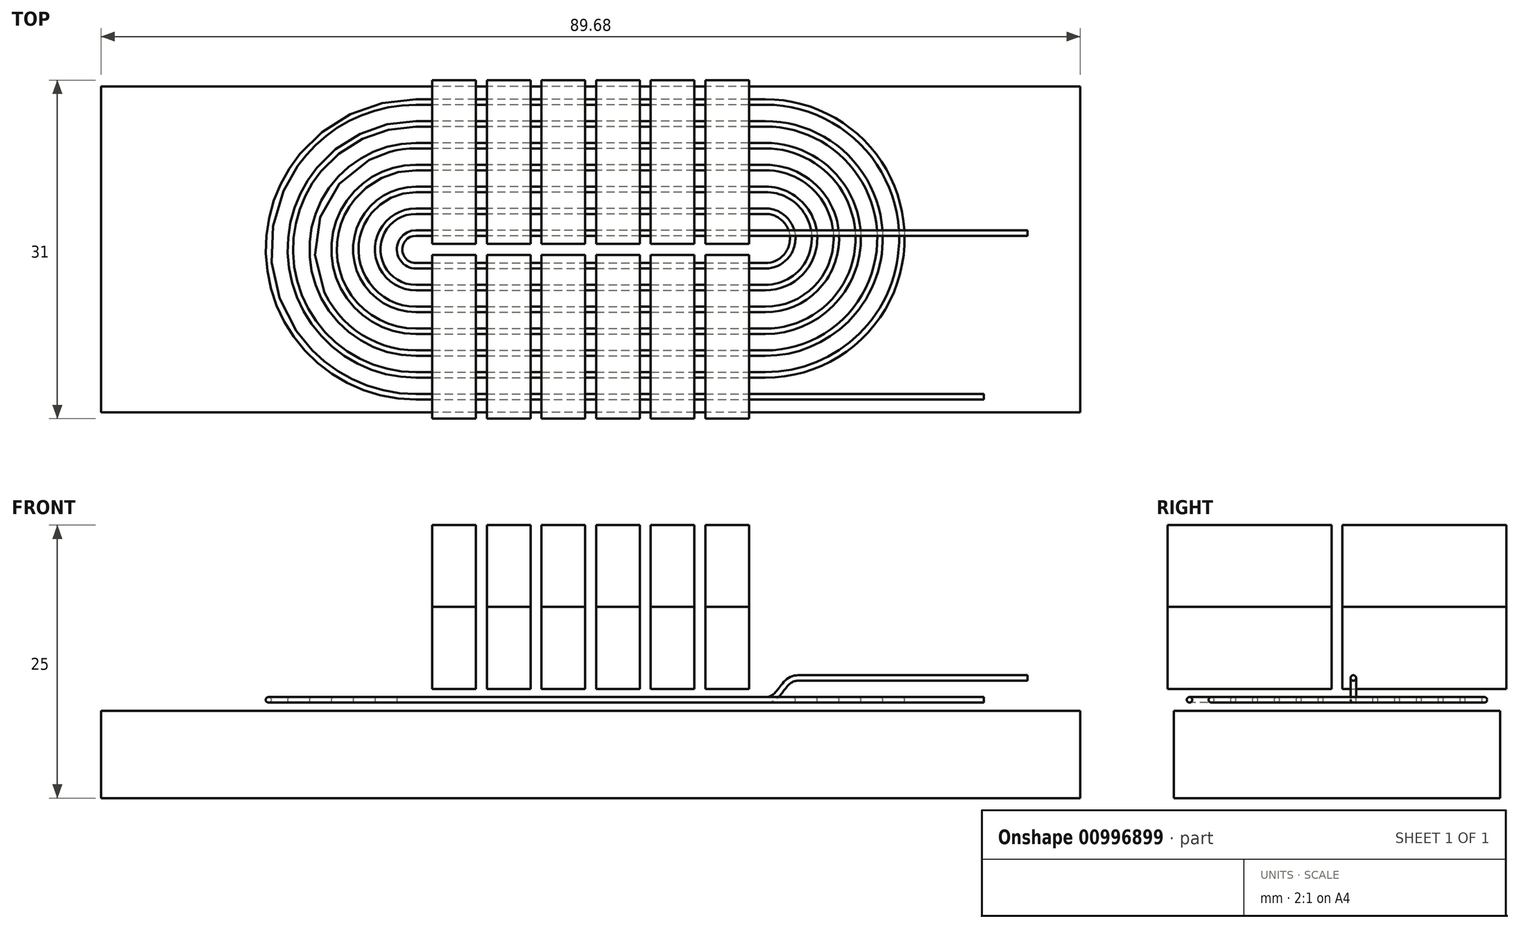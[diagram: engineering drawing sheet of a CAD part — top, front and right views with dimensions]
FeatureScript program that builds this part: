
annotation { "Feature Type Name" : "Feature", "Feature Type Description" : "" }
export const myFeature = defineFeature(function(context is Context, id is Id, definition is map)
    precondition{}
    {
        {
            var Q0;
            Q0=qCreatedBy(makeId("Top.planeOp"),FACE);
            cPlane(context, id + "F0", {"entities" : qUnion([Q0]), "cplaneType" : CPlaneType.OFFSET, "offset" : 1 * mm, "width" : 150 * mm, "height" : 150 * mm});
        }
        {
            var Q0;
            Q0=qCreatedBy(id+"F0.planeOp",FACE);
            var sketch = newSketch(context, id + "F1", { "sketchPlane" : qUnion([Q0])});
            skPoint(sketch, "E0.middle", {"position": v(0, 0) * mm});
            skLineSegment(sketch, "E1", {"start": v(0, 0) * mm, "end": v(0, 4.02) * mm, "construction": true});
            skLineSegment(sketch, "E2", {"start": v(0, 0) * mm, "end": v(5, 0) * mm, "construction": true});
            skPoint(sketch, "E3", {"position": v(0.5, 0.5) * mm});
            skLineSegment(sketch, "E4.bottom", {"start": v(0.5, 0.5) * mm, "end": v(4.5, 0.5) * mm});
            skLineSegment(sketch, "E4.top", {"start": v(0.5, 15.5) * mm, "end": v(4.5, 15.5) * mm});
            skLineSegment(sketch, "E4.left", {"start": v(0.5, 0.5) * mm, "end": v(0.5, 15.5) * mm});
            skLineSegment(sketch, "E4.right", {"start": v(4.5, 0.5) * mm, "end": v(4.5, 15.5) * mm});
            skLineSegment(sketch, "E5", {"start": v(5, 0) * mm, "end": v(5, 16.05) * mm, "construction": true});
            skLineSegment(sketch, "E6.MirrorCS", {"start": v(5.5, 0.5) * mm, "end": v(5.5, 15.5) * mm});
            skLineSegment(sketch, "E7.MirrorCS", {"start": v(9.5, 15.5) * mm, "end": v(5.5, 15.5) * mm});
            skLineSegment(sketch, "E8.MirrorCS", {"start": v(9.5, 0.5) * mm, "end": v(9.5, 15.5) * mm});
            skLineSegment(sketch, "E9.MirrorCS", {"start": v(9.5, 0.5) * mm, "end": v(5.5, 0.5) * mm});
            skLineSegment(sketch, "E10", {"start": v(7.5, 0.5) * mm, "end": v(7.5, 15.5) * mm, "construction": true});
            skLineSegment(sketch, "E11.MirrorCS", {"start": v(10.5, 0.5) * mm, "end": v(10.5, 15.5) * mm});
            skLineSegment(sketch, "E12.MirrorCS", {"start": v(14.5, 15.5) * mm, "end": v(10.5, 15.5) * mm});
            skLineSegment(sketch, "E13.MirrorCS", {"start": v(14.5, 0.5) * mm, "end": v(14.5, 15.5) * mm});
            skLineSegment(sketch, "E14.MirrorCS", {"start": v(14.5, 0.5) * mm, "end": v(10.5, 0.5) * mm});
            skLineSegment(sketch, "E15.MirrorCS", {"start": v(-10.5, 0.5) * mm, "end": v(-10.5, 15.5) * mm});
            skLineSegment(sketch, "E16.MirrorCS", {"start": v(-14.5, 0.5) * mm, "end": v(-14.5, 15.5) * mm});
            skLineSegment(sketch, "E17.MirrorCS", {"start": v(-0.5, 15.5) * mm, "end": v(-4.5, 15.5) * mm});
            skLineSegment(sketch, "E18.MirrorCS", {"start": v(-9.5, 0.5) * mm, "end": v(-9.5, 15.5) * mm});
            skLineSegment(sketch, "E19.MirrorCS", {"start": v(-5, 0) * mm, "end": v(-5, 16.05) * mm, "construction": true});
            skLineSegment(sketch, "E20.MirrorCS", {"start": v(-14.5, 15.5) * mm, "end": v(-10.5, 15.5) * mm});
            skLineSegment(sketch, "E21.MirrorCS", {"start": v(-14.5, 0.5) * mm, "end": v(-10.5, 0.5) * mm});
            skLineSegment(sketch, "E22.MirrorCS", {"start": v(-0.5, 0.5) * mm, "end": v(-0.5, 15.5) * mm});
            skLineSegment(sketch, "E23.MirrorCS", {"start": v(-5.5, 0.5) * mm, "end": v(-5.5, 15.5) * mm});
            skLineSegment(sketch, "E24.MirrorCS", {"start": v(-7.5, 0.5) * mm, "end": v(-7.5, 15.5) * mm, "construction": true});
            skLineSegment(sketch, "E25.MirrorCS", {"start": v(-4.5, 0.5) * mm, "end": v(-4.5, 15.5) * mm});
            skPoint(sketch, "E26.MirrorP", {"position": v(-0.5, 0.5) * mm});
            skLineSegment(sketch, "E27.MirrorCS", {"start": v(-0.5, 0.5) * mm, "end": v(-4.5, 0.5) * mm});
            skLineSegment(sketch, "E28.MirrorCS", {"start": v(-9.5, 0.5) * mm, "end": v(-5.5, 0.5) * mm});
            skLineSegment(sketch, "E29.MirrorCS", {"start": v(-9.5, 15.5) * mm, "end": v(-5.5, 15.5) * mm});
            skLineSegment(sketch, "E30.MirrorCS", {"start": v(10.5, -0.5) * mm, "end": v(10.5, -15.5) * mm});
            skLineSegment(sketch, "E31.MirrorCS", {"start": v(7.5, -0.5) * mm, "end": v(7.5, -15.5) * mm, "construction": true});
            skLineSegment(sketch, "E32.MirrorCS", {"start": v(14.5, -0.5) * mm, "end": v(14.5, -15.5) * mm});
            skLineSegment(sketch, "E33.MirrorCS", {"start": v(-10.5, -0.5) * mm, "end": v(-10.5, -15.5) * mm});
            skPoint(sketch, "E34.MirrorP", {"position": v(-0.5, -0.5) * mm});
            skLineSegment(sketch, "E35.MirrorCS", {"start": v(9.5, -0.5) * mm, "end": v(5.5, -0.5) * mm});
            skLineSegment(sketch, "E36.MirrorCS", {"start": v(-14.5, -0.5) * mm, "end": v(-14.5, -15.5) * mm});
            skLineSegment(sketch, "E37.MirrorCS", {"start": v(14.5, -15.5) * mm, "end": v(10.5, -15.5) * mm});
            skLineSegment(sketch, "E38.MirrorCS", {"start": v(9.5, -0.5) * mm, "end": v(9.5, -15.5) * mm});
            skLineSegment(sketch, "E39.MirrorCS", {"start": v(-0.5, -15.5) * mm, "end": v(-4.5, -15.5) * mm});
            skLineSegment(sketch, "E40.MirrorCS", {"start": v(14.5, -0.5) * mm, "end": v(10.5, -0.5) * mm});
            skLineSegment(sketch, "E41.MirrorCS", {"start": v(9.5, -15.5) * mm, "end": v(5.5, -15.5) * mm});
            skLineSegment(sketch, "E42.MirrorCS", {"start": v(-9.5, -0.5) * mm, "end": v(-9.5, -15.5) * mm});
            skPoint(sketch, "E43.MirrorP", {"position": v(0.5, -0.5) * mm});
            skLineSegment(sketch, "E44.MirrorCS", {"start": v(5.5, -0.5) * mm, "end": v(5.5, -15.5) * mm});
            skLineSegment(sketch, "E45.MirrorCS", {"start": v(-0.5, -0.5) * mm, "end": v(-4.5, -0.5) * mm});
            skLineSegment(sketch, "E46.MirrorCS", {"start": v(-9.5, -0.5) * mm, "end": v(-5.5, -0.5) * mm});
            skLineSegment(sketch, "E47.MirrorCS", {"start": v(-14.5, -0.5) * mm, "end": v(-10.5, -0.5) * mm});
            skLineSegment(sketch, "E48.MirrorCS", {"start": v(-9.5, -15.5) * mm, "end": v(-5.5, -15.5) * mm});
            skLineSegment(sketch, "E49.MirrorCS", {"start": v(-14.5, -15.5) * mm, "end": v(-10.5, -15.5) * mm});
            skLineSegment(sketch, "E50.MirrorCS", {"start": v(0.5, -15.5) * mm, "end": v(4.5, -15.5) * mm});
            skLineSegment(sketch, "E51.MirrorCS", {"start": v(5, 0) * mm, "end": v(5, -16.05) * mm, "construction": true});
            skLineSegment(sketch, "E52.MirrorCS", {"start": v(-0.5, -0.5) * mm, "end": v(-0.5, -15.5) * mm});
            skLineSegment(sketch, "E53.MirrorCS", {"start": v(4.5, -0.5) * mm, "end": v(4.5, -15.5) * mm});
            skLineSegment(sketch, "E54.MirrorCS", {"start": v(-5.5, -0.5) * mm, "end": v(-5.5, -15.5) * mm});
            skLineSegment(sketch, "E55.MirrorCS", {"start": v(-4.5, -0.5) * mm, "end": v(-4.5, -15.5) * mm});
            skLineSegment(sketch, "E56.MirrorCS", {"start": v(0.5, -0.5) * mm, "end": v(0.5, -15.5) * mm});
            skLineSegment(sketch, "E57.MirrorCS", {"start": v(-5, 0) * mm, "end": v(-5, -16.05) * mm, "construction": true});
            skLineSegment(sketch, "E58.MirrorCS", {"start": v(0.5, -0.5) * mm, "end": v(4.5, -0.5) * mm});
            skLineSegment(sketch, "E59.MirrorCS", {"start": v(0, 0) * mm, "end": v(0, -4.02) * mm, "construction": true});
            skLineSegment(sketch, "E60.MirrorCS", {"start": v(-7.5, -0.5) * mm, "end": v(-7.5, -15.5) * mm, "construction": true});
            skSolve(sketch);
        }
        {
            var Q0;
            Q0=qCreatedBy(makeId("Top.planeOp"),FACE);
            var sketch = newSketch(context, id + "F2", { "sketchPlane" : qUnion([Q0])});
            skLineSegment(sketch, "E61", {"start": v(16, 1.5) * mm, "end": v(0, 1.5) * mm});
            skLineSegment(sketch, "E62", {"start": v(0, 1.5) * mm, "end": v(-16, 1.5) * mm});
            skLineSegment(sketch, "E63.MirrorCS", {"start": v(0, -1.5) * mm, "end": v(-16, -1.5) * mm});
            skLineSegment(sketch, "E64.MirrorCS", {"start": v(0, -1.5) * mm, "end": v(16, -1.5) * mm});
            skArc(sketch, "E65", {"start": v(-16, 1.5) * mm, "mid": v(-17.5, 0) * mm, "end": v(-16, -1.5) * mm});
            skArc(sketch, "E66", {"start": v(16, -1.5) * mm, "mid": v(18.5, 1) * mm, "end": v(16, 3.5) * mm});
            skLineSegment(sketch, "E67", {"start": v(16, 3.5) * mm, "end": v(16, 1) * mm, "construction": true});
            skLineSegment(sketch, "E68", {"start": v(16, 1.5) * mm, "end": v(36, 1.5) * mm});
            skArc(sketch, "E69.0", {"start": v(16, -3.5) * mm, "mid": v(20.5, 1) * mm, "end": v(16, 5.5) * mm});
            skLineSegment(sketch, "E69.1", {"start": v(0, -3.5) * mm, "end": v(16, -3.5) * mm});
            skLineSegment(sketch, "E69.2", {"start": v(16, 3.5) * mm, "end": v(0, 3.5) * mm});
            skLineSegment(sketch, "E69.3", {"start": v(0, 3.5) * mm, "end": v(-16, 3.5) * mm});
            skArc(sketch, "E69.4", {"start": v(-16, 3.5) * mm, "mid": v(-19.5, 0) * mm, "end": v(-16, -3.5) * mm});
            skLineSegment(sketch, "E69.5", {"start": v(0, -3.5) * mm, "end": v(-16, -3.5) * mm});
            skArc(sketch, "E70.0", {"start": v(16, -5.5) * mm, "mid": v(22.5, 1) * mm, "end": v(16, 7.5) * mm});
            skLineSegment(sketch, "E70.1", {"start": v(0, -5.5) * mm, "end": v(16, -5.5) * mm});
            skLineSegment(sketch, "E70.2", {"start": v(16, 5.5) * mm, "end": v(0, 5.5) * mm});
            skLineSegment(sketch, "E70.3", {"start": v(0, 5.5) * mm, "end": v(-16, 5.5) * mm});
            skArc(sketch, "E70.4", {"start": v(-16, 5.5) * mm, "mid": v(-21.5, 0) * mm, "end": v(-16, -5.5) * mm});
            skLineSegment(sketch, "E70.5", {"start": v(0, -5.5) * mm, "end": v(-16, -5.5) * mm});
            skArc(sketch, "E71.0", {"start": v(16, -7.5) * mm, "mid": v(24.5, 1) * mm, "end": v(16, 9.5) * mm});
            skLineSegment(sketch, "E71.1", {"start": v(0, -7.5) * mm, "end": v(16, -7.5) * mm});
            skLineSegment(sketch, "E71.2", {"start": v(16, 7.5) * mm, "end": v(0, 7.5) * mm});
            skLineSegment(sketch, "E71.3", {"start": v(0, 7.5) * mm, "end": v(-16, 7.5) * mm});
            skArc(sketch, "E71.4", {"start": v(-16, 7.5) * mm, "mid": v(-23.5, 0) * mm, "end": v(-16, -7.5) * mm});
            skLineSegment(sketch, "E71.5", {"start": v(0, -7.5) * mm, "end": v(-16, -7.5) * mm});
            skArc(sketch, "E72.0", {"start": v(16, -9.5) * mm, "mid": v(26.5, 1) * mm, "end": v(16, 11.5) * mm});
            skLineSegment(sketch, "E72.1", {"start": v(0, -9.5) * mm, "end": v(16, -9.5) * mm});
            skLineSegment(sketch, "E72.2", {"start": v(0, -9.5) * mm, "end": v(-16, -9.5) * mm});
            skArc(sketch, "E72.3", {"start": v(-16, 9.5) * mm, "mid": v(-25.5, 0) * mm, "end": v(-16, -9.5) * mm});
            skLineSegment(sketch, "E73.0", {"start": v(0, 9.5) * mm, "end": v(-16, 9.5) * mm});
            skLineSegment(sketch, "E73.1", {"start": v(16, 9.5) * mm, "end": v(0, 9.5) * mm});
            skArc(sketch, "E74.0", {"start": v(16, -11.5) * mm, "mid": v(28.5, 1) * mm, "end": v(16, 13.5) * mm});
            skLineSegment(sketch, "E74.1", {"start": v(0, -11.5) * mm, "end": v(16, -11.5) * mm});
            skLineSegment(sketch, "E74.2", {"start": v(16, 11.5) * mm, "end": v(0, 11.5) * mm});
            skLineSegment(sketch, "E74.3", {"start": v(0, 11.5) * mm, "end": v(-16, 11.5) * mm});
            skArc(sketch, "E74.4", {"start": v(-16, 11.5) * mm, "mid": v(-27.5, 0) * mm, "end": v(-16, -11.5) * mm});
            skLineSegment(sketch, "E74.5", {"start": v(0, -11.5) * mm, "end": v(-16, -11.5) * mm});
            skLineSegment(sketch, "E75.1", {"start": v(0, -13.5) * mm, "end": v(16, -13.5) * mm});
            skLineSegment(sketch, "E75.2", {"start": v(16, 13.5) * mm, "end": v(0, 13.5) * mm});
            skLineSegment(sketch, "E75.3", {"start": v(0, 13.5) * mm, "end": v(-16, 13.5) * mm});
            skArc(sketch, "E75.4", {"start": v(-16, 13.5) * mm, "mid": v(-29.5, 0) * mm, "end": v(-16, -13.5) * mm});
            skLineSegment(sketch, "E75.5", {"start": v(0, -13.5) * mm, "end": v(-16, -13.5) * mm});
            skLineSegment(sketch, "E76", {"start": v(16, -13.5) * mm, "end": v(36, -13.5) * mm});
            skSolve(sketch);
        }
        {
            var Q0;
            Q0=sQuery(id+"F2.wireOp",EDGE,"E68");
            cPlane(context, id + "F3", {"entities" : qUnion([Q0]), "cplaneType" : CPlaneType.LINE_ANGLE, "offset" : 25 * mm, "angle" : 0 * degree, "width" : 150 * mm, "height" : 150 * mm});
        }
        {
            var Q0;
            Q0=qCreatedBy(makeId("Right.planeOp"),FACE);
            var sketch = newSketch(context, id + "F4", { "sketchPlane" : qUnion([Q0])});
            skCircle(sketch, "E77", {"center": v(-13.5, 0) * mm, "radius": 0.25 * mm});
            skSolve(sketch);
        }
        {
            var Q0;
            Q0=makeQuery(id+"F4.imprint","IMPRINT",FACE,{"disambiguationData":[TD([[makeQuery(id+"F4.imprint","IMPRINT",EDGE,{"derivedFrom":sQuery(id+"F4.wireOp",EDGE,"E77")}),1.0]])]});
            var Q1;
            Q1=sQuery(id+"F2.wireOp",EDGE,"E75.1");
            var Q2;
            Q2=sQuery(id+"F2.wireOp",EDGE,"E76");
            var Q3;
            Q3=sQuery(id+"F2.wireOp",EDGE,"E75.5");
            var Q4;
            Q4=sQuery(id+"F2.wireOp",EDGE,"E75.4");
            var Q5;
            Q5=sQuery(id+"F2.wireOp",EDGE,"E75.3");
            var Q6;
            Q6=sQuery(id+"F2.wireOp",EDGE,"E75.2");
            var Q7;
            Q7=sQuery(id+"F2.wireOp",EDGE,"E74.0");
            var Q8;
            Q8=sQuery(id+"F2.wireOp",EDGE,"E74.1");
            var Q9;
            Q9=sQuery(id+"F2.wireOp",EDGE,"E74.5");
            var Q10;
            Q10=sQuery(id+"F2.wireOp",EDGE,"E74.4");
            var Q11;
            Q11=sQuery(id+"F2.wireOp",EDGE,"E74.3");
            var Q12;
            Q12=sQuery(id+"F2.wireOp",EDGE,"E74.2");
            var Q13;
            Q13=sQuery(id+"F2.wireOp",EDGE,"E72.0");
            var Q14;
            Q14=sQuery(id+"F2.wireOp",EDGE,"E72.1");
            var Q15;
            Q15=sQuery(id+"F2.wireOp",EDGE,"E72.2");
            var Q16;
            Q16=sQuery(id+"F2.wireOp",EDGE,"E72.3");
            var Q17;
            Q17=sQuery(id+"F2.wireOp",EDGE,"E73.0");
            var Q18;
            Q18=sQuery(id+"F2.wireOp",EDGE,"E71.0");
            var Q19;
            Q19=sQuery(id+"F2.wireOp",EDGE,"E71.1");
            var Q20;
            Q20=sQuery(id+"F2.wireOp",EDGE,"E71.5");
            var Q21;
            Q21=sQuery(id+"F2.wireOp",EDGE,"E71.4");
            var Q22;
            Q22=sQuery(id+"F2.wireOp",EDGE,"E71.3");
            var Q23;
            Q23=sQuery(id+"F2.wireOp",EDGE,"E71.2");
            var Q24;
            Q24=sQuery(id+"F2.wireOp",EDGE,"E73.1");
            var Q25;
            Q25=sQuery(id+"F2.wireOp",EDGE,"E70.0");
            var Q26;
            Q26=sQuery(id+"F2.wireOp",EDGE,"E70.1");
            var Q27;
            Q27=sQuery(id+"F2.wireOp",EDGE,"E70.4");
            var Q28;
            Q28=sQuery(id+"F2.wireOp",EDGE,"E70.3");
            var Q29;
            Q29=sQuery(id+"F2.wireOp",EDGE,"E70.2");
            var Q30;
            Q30=sQuery(id+"F2.wireOp",EDGE,"E69.0");
            var Q31;
            Q31=sQuery(id+"F2.wireOp",EDGE,"E69.1");
            var Q32;
            Q32=sQuery(id+"F2.wireOp",EDGE,"E69.5");
            var Q33;
            Q33=sQuery(id+"F2.wireOp",EDGE,"E69.4");
            var Q34;
            Q34=sQuery(id+"F2.wireOp",EDGE,"E69.3");
            var Q35;
            Q35=sQuery(id+"F2.wireOp",EDGE,"E70.5");
            var Q36;
            Q36=sQuery(id+"F2.wireOp",EDGE,"E69.2");
            var Q37;
            Q37=sQuery(id+"F2.wireOp",EDGE,"E66");
            var Q38;
            Q38=sQuery(id+"F2.wireOp",EDGE,"E64.MirrorCS");
            var Q39;
            Q39=sQuery(id+"F2.wireOp",EDGE,"E63.MirrorCS");
            var Q40;
            Q40=sQuery(id+"F2.wireOp",EDGE,"E65");
            var Q41;
            Q41=sQuery(id+"F2.wireOp",EDGE,"E62");
            var Q42;
            Q42=sQuery(id+"F2.wireOp",EDGE,"E61");
            sweep(context, id + "F5", {"profiles" : qUnion([Q0]), "path" : qUnion([Q1, Q2, Q3, Q4, Q5, Q6, Q7, Q8, Q9, Q10, Q11, Q12, Q13, Q14, Q15, Q16, Q17, Q18, Q19, Q20, Q21, Q22, Q23, Q24, Q25, Q26, Q27, Q28, Q29, Q30, Q31, Q32, Q33, Q34, Q35, Q36, Q37, Q38, Q39, Q40, Q41, Q42])});
        }
        {
            var Q0;
            Q0=qCreatedBy(id+"F3.planeOp",FACE);
            var sketch = newSketch(context, id + "F6", { "sketchPlane" : qUnion([Q0])});
            skLineSegment(sketch, "E78.0", {"start": v(-19, 2) * mm, "end": v(-40, 2) * mm});
            skLineSegment(sketch, "E79", {"start": v(-19, 2) * mm, "end": v(-16, 2) * mm, "construction": true});
            skLineSegment(sketch, "E80", {"start": v(-17.5, 2) * mm, "end": v(-17.5, 0) * mm, "construction": true});
            skPoint(sketch, "E81", {"position": v(-17.5, 1) * mm});
            skFitSpline(sketch, "E82", {"points": [v(-16, 0) * mm, v(-17.5, 1) * mm, v(-19, 2) * mm], "startDerivative": vector(-4.5, 0) * mm, "endDerivative": vector(-4.5, 0) * mm});
            skLineSegment(sketch, "E83", {"start": v(-17.5, 2) * mm, "end": v(-19, 2) * mm, "construction": true});
            skLineSegment(sketch, "E84", {"start": v(-17.5, 0) * mm, "end": v(-16, 0) * mm, "construction": true});
            skSolve(sketch);
        }
        {
            var Q0;
            Q0=makeQuery(id+"F5.opSweep","CAP_FACE",FACE,{"disambiguationData":[OSD([sQuery(id+"F2.wireOp",VERTEX,"E61.start"),sQuery(id+"F4.wireOp",EDGE,"E77")])],"isStart":true});
            var Q1;
            Q1=sQuery(id+"F6.wireOp",EDGE,"E82");
            var Q2;
            Q2=sQuery(id+"F6.wireOp",EDGE,"E78.0");
            sweep(context, id + "F7", {"operationType" : NewBodyOperationType.ADD, "profiles" : qUnion([Q0]), "path" : qUnion([Q1, Q2])});
        }
        {
            var Q0;
            Q0=makeQuery(id+"F1.imprint","IMPRINT",FACE,{"disambiguationData":[TD([[makeQuery(id+"F1.imprint","IMPRINT",EDGE,{"derivedFrom":sQuery(id+"F1.wireOp",EDGE,"E33.MirrorCS")}),-1.0]])]});
            var Q1;
            Q1=makeQuery(id+"F1.imprint","IMPRINT",FACE,{"disambiguationData":[TD([[makeQuery(id+"F1.imprint","IMPRINT",EDGE,{"derivedFrom":sQuery(id+"F1.wireOp",EDGE,"E42.MirrorCS")}),1.0]])]});
            var Q2;
            Q2=makeQuery(id+"F1.imprint","IMPRINT",FACE,{"disambiguationData":[TD([[makeQuery(id+"F1.imprint","IMPRINT",EDGE,{"derivedFrom":sQuery(id+"F1.wireOp",EDGE,"E39.MirrorCS")}),-1.0]])]});
            var Q3;
            Q3=makeQuery(id+"F1.imprint","IMPRINT",FACE,{"disambiguationData":[TD([[makeQuery(id+"F1.imprint","IMPRINT",EDGE,{"derivedFrom":sQuery(id+"F1.wireOp",EDGE,"E50.MirrorCS")}),1.0]])]});
            var Q4;
            Q4=makeQuery(id+"F1.imprint","IMPRINT",FACE,{"disambiguationData":[TD([[makeQuery(id+"F1.imprint","IMPRINT",EDGE,{"derivedFrom":sQuery(id+"F1.wireOp",EDGE,"E35.MirrorCS")}),1.0]])]});
            var Q5;
            Q5=makeQuery(id+"F1.imprint","IMPRINT",FACE,{"disambiguationData":[TD([[makeQuery(id+"F1.imprint","IMPRINT",EDGE,{"derivedFrom":sQuery(id+"F1.wireOp",EDGE,"E30.MirrorCS")}),1.0]])]});
            var Q6;
            Q6=makeQuery(id+"F1.imprint","IMPRINT",FACE,{"disambiguationData":[TD([[makeQuery(id+"F1.imprint","IMPRINT",EDGE,{"derivedFrom":sQuery(id+"F1.wireOp",EDGE,"E11.MirrorCS")}),-1.0]])]});
            var Q7;
            Q7=makeQuery(id+"F1.imprint","IMPRINT",FACE,{"disambiguationData":[TD([[makeQuery(id+"F1.imprint","IMPRINT",EDGE,{"derivedFrom":sQuery(id+"F1.wireOp",EDGE,"E6.MirrorCS")}),-1.0]])]});
            var Q8;
            Q8=makeQuery(id+"F1.imprint","IMPRINT",FACE,{"disambiguationData":[TD([[makeQuery(id+"F1.imprint","IMPRINT",EDGE,{"derivedFrom":sQuery(id+"F1.wireOp",EDGE,"E4.bottom")}),1.0]])]});
            var Q9;
            Q9=makeQuery(id+"F1.imprint","IMPRINT",FACE,{"disambiguationData":[TD([[makeQuery(id+"F1.imprint","IMPRINT",EDGE,{"derivedFrom":sQuery(id+"F1.wireOp",EDGE,"E17.MirrorCS")}),1.0]])]});
            var Q10;
            Q10=makeQuery(id+"F1.imprint","IMPRINT",FACE,{"disambiguationData":[TD([[makeQuery(id+"F1.imprint","IMPRINT",EDGE,{"derivedFrom":sQuery(id+"F1.wireOp",EDGE,"E18.MirrorCS")}),-1.0]])]});
            var Q11;
            Q11=makeQuery(id+"F1.imprint","IMPRINT",FACE,{"disambiguationData":[TD([[makeQuery(id+"F1.imprint","IMPRINT",EDGE,{"derivedFrom":sQuery(id+"F1.wireOp",EDGE,"E15.MirrorCS")}),1.0]])]});
            extrude(context, id + "F8", {"entities" : qUnion([Q0, Q1, Q2, Q3, Q4, Q5, Q6, Q7, Q8, Q9, Q10, Q11]), "depth" : 7.5 * mm, "offsetDistance" : 25 * mm});
        }
        {
            var Q0;
            Q0=makeQuery(id+"F8.opExtrude","SWEPT_BODY",BODY,{"disambiguationData":[OSD([sQuery(id+"F1.wireOp",EDGE,"E15.MirrorCS"),sQuery(id+"F1.wireOp",EDGE,"E16.MirrorCS"),sQuery(id+"F1.wireOp",EDGE,"E20.MirrorCS"),sQuery(id+"F1.wireOp",EDGE,"E21.MirrorCS")])]});
            var Q1;
            Q1=makeQuery(id+"F8.opExtrude","SWEPT_BODY",BODY,{"disambiguationData":[OSD([sQuery(id+"F1.wireOp",EDGE,"E18.MirrorCS"),sQuery(id+"F1.wireOp",EDGE,"E23.MirrorCS"),sQuery(id+"F1.wireOp",EDGE,"E28.MirrorCS"),sQuery(id+"F1.wireOp",EDGE,"E29.MirrorCS")])]});
            var Q2;
            Q2=makeQuery(id+"F8.opExtrude","SWEPT_BODY",BODY,{"disambiguationData":[OSD([sQuery(id+"F1.wireOp",EDGE,"E17.MirrorCS"),sQuery(id+"F1.wireOp",EDGE,"E22.MirrorCS"),sQuery(id+"F1.wireOp",EDGE,"E25.MirrorCS"),sQuery(id+"F1.wireOp",EDGE,"E27.MirrorCS")])]});
            var Q3;
            Q3=makeQuery(id+"F8.opExtrude","SWEPT_BODY",BODY,{"disambiguationData":[OSD([sQuery(id+"F1.wireOp",EDGE,"E4.bottom"),sQuery(id+"F1.wireOp",EDGE,"E4.top"),sQuery(id+"F1.wireOp",EDGE,"E4.left"),sQuery(id+"F1.wireOp",EDGE,"E4.right")])]});
            var Q4;
            Q4=makeQuery(id+"F8.opExtrude","SWEPT_BODY",BODY,{"disambiguationData":[OSD([sQuery(id+"F1.wireOp",EDGE,"E11.MirrorCS"),sQuery(id+"F1.wireOp",EDGE,"E12.MirrorCS"),sQuery(id+"F1.wireOp",EDGE,"E13.MirrorCS"),sQuery(id+"F1.wireOp",EDGE,"E14.MirrorCS")])]});
            var Q5;
            Q5=makeQuery(id+"F8.opExtrude","SWEPT_BODY",BODY,{"disambiguationData":[OSD([sQuery(id+"F1.wireOp",EDGE,"E6.MirrorCS"),sQuery(id+"F1.wireOp",EDGE,"E7.MirrorCS"),sQuery(id+"F1.wireOp",EDGE,"E8.MirrorCS"),sQuery(id+"F1.wireOp",EDGE,"E9.MirrorCS")])]});
            var Q6;
            Q6=makeQuery(id+"F8.opExtrude","SWEPT_BODY",BODY,{"disambiguationData":[OSD([sQuery(id+"F1.wireOp",EDGE,"E30.MirrorCS"),sQuery(id+"F1.wireOp",EDGE,"E32.MirrorCS"),sQuery(id+"F1.wireOp",EDGE,"E37.MirrorCS"),sQuery(id+"F1.wireOp",EDGE,"E40.MirrorCS")])]});
            var Q7;
            Q7=makeQuery(id+"F8.opExtrude","SWEPT_BODY",BODY,{"disambiguationData":[OSD([sQuery(id+"F1.wireOp",EDGE,"E35.MirrorCS"),sQuery(id+"F1.wireOp",EDGE,"E38.MirrorCS"),sQuery(id+"F1.wireOp",EDGE,"E41.MirrorCS"),sQuery(id+"F1.wireOp",EDGE,"E44.MirrorCS")])]});
            var Q8;
            Q8=makeQuery(id+"F8.opExtrude","SWEPT_BODY",BODY,{"disambiguationData":[OSD([sQuery(id+"F1.wireOp",EDGE,"E39.MirrorCS"),sQuery(id+"F1.wireOp",EDGE,"E45.MirrorCS"),sQuery(id+"F1.wireOp",EDGE,"E52.MirrorCS"),sQuery(id+"F1.wireOp",EDGE,"E55.MirrorCS")])]});
            var Q9;
            Q9=makeQuery(id+"F8.opExtrude","SWEPT_BODY",BODY,{"disambiguationData":[OSD([sQuery(id+"F1.wireOp",EDGE,"E42.MirrorCS"),sQuery(id+"F1.wireOp",EDGE,"E46.MirrorCS"),sQuery(id+"F1.wireOp",EDGE,"E48.MirrorCS"),sQuery(id+"F1.wireOp",EDGE,"E54.MirrorCS")])]});
            var Q10;
            Q10=makeQuery(id+"F8.opExtrude","SWEPT_BODY",BODY,{"disambiguationData":[OSD([sQuery(id+"F1.wireOp",EDGE,"E33.MirrorCS"),sQuery(id+"F1.wireOp",EDGE,"E36.MirrorCS"),sQuery(id+"F1.wireOp",EDGE,"E47.MirrorCS"),sQuery(id+"F1.wireOp",EDGE,"E49.MirrorCS")])]});
            var Q11;
            Q11=makeQuery(id+"F8.opExtrude","SWEPT_BODY",BODY,{"disambiguationData":[OSD([sQuery(id+"F1.wireOp",EDGE,"E50.MirrorCS"),sQuery(id+"F1.wireOp",EDGE,"E53.MirrorCS"),sQuery(id+"F1.wireOp",EDGE,"E56.MirrorCS"),sQuery(id+"F1.wireOp",EDGE,"E58.MirrorCS")])]});
            var Q12;
            Q12=makeQuery(id+"F8.opExtrude","CAP_FACE",FACE,{"disambiguationData":[OSD([sQuery(id+"F1.wireOp",EDGE,"E33.MirrorCS"),sQuery(id+"F1.wireOp",EDGE,"E36.MirrorCS"),sQuery(id+"F1.wireOp",EDGE,"E47.MirrorCS"),sQuery(id+"F1.wireOp",EDGE,"E49.MirrorCS")])],"isStart":false});
            mirror(context, id + "F9", {"entities" : qUnion([Q0, Q1, Q2, Q3, Q4, Q5, Q6, Q7, Q8, Q9, Q10, Q11]), "mirrorPlane" : qUnion([Q12])});
        }
        {
            var Q0;
            Q0=qCreatedBy(makeId("Top.planeOp"),FACE);
            cPlane(context, id + "F10", {"entities" : qUnion([Q0]), "cplaneType" : CPlaneType.OFFSET, "offset" : 1 * mm, "oppositeDirection" : true, "width" : 150 * mm, "height" : 150 * mm});
        }
        {
            var Q0;
            Q0=qCreatedBy(id+"F10.planeOp",FACE);
            var sketch = newSketch(context, id + "F11", { "sketchPlane" : qUnion([Q0])});
            skLineSegment(sketch, "E85.bottom", {"start": v(44.84, 14.93) * mm, "end": v(-44.84, 14.93) * mm});
            skLineSegment(sketch, "E85.top", {"start": v(44.84, -14.93) * mm, "end": v(-44.84, -14.93) * mm});
            skLineSegment(sketch, "E85.left", {"start": v(44.84, 14.93) * mm, "end": v(44.84, -14.93) * mm});
            skLineSegment(sketch, "E85.right", {"start": v(-44.84, 14.93) * mm, "end": v(-44.84, -14.93) * mm});
            skPoint(sketch, "E85.middle", {"position": v(0, 0) * mm});
            skSolve(sketch);
        }
        {
            var Q0;
            Q0=makeQuery(id+"F11.imprint","IMPRINT",FACE,{"disambiguationData":[TD([[makeQuery(id+"F11.imprint","IMPRINT",EDGE,{"derivedFrom":sQuery(id+"F11.wireOp",EDGE,"E85.bottom")}),1.0]])]});
            extrude(context, id + "F12", {"entities" : qUnion([Q0]), "operationType" : NewBodyOperationType.ADD, "oppositeDirection" : true, "depth" : 8 * mm, "offsetDistance" : 25 * mm});
        }
        {
            var Q0;
            Q0=makeQuery(id+"F12.opExtrude","SWEPT_FACE",FACE,{"disambiguationData":[OSD([sQuery(id+"F11.wireOp",EDGE,"E85.top")])]});
            var sketch = newSketch(context, id + "F13", { "sketchPlane" : qUnion([Q0])});
            skLineSegment(sketch, "E86", {"start": v(44.84, -5) * mm, "end": v(-44.84, -5) * mm, "construction": true});
            skSolve(sketch);
        }
        {
            var Q0;
            Q0=sQuery(id+"F13.wireOp",EDGE,"E86");
            cPlane(context, id + "F14", {"entities" : qUnion([Q0]), "cplaneType" : CPlaneType.LINE_ANGLE, "offset" : 25 * mm, "angle" : 90 * degree, "width" : 150 * mm, "height" : 150 * mm});
        }
        {
            var Q0;
            Q0=qCreatedBy(id+"F14.planeOp",FACE);
            var sketch = newSketch(context, id + "F15", { "sketchPlane" : qUnion([Q0])});
            skLineSegment(sketch, "E87", {"start": v(0, 0) * mm, "end": v(0, -44.18) * mm});
            skLineSegment(sketch, "E88", {"start": v(0, 0) * mm, "end": v(63.24, 0) * mm});
            skSolve(sketch);
        }
        {
            var Q0;
            Q0=sQuery(id+"F15.wireOp",EDGE,"E88");
            cPlane(context, id + "F16", {"entities" : qUnion([Q0]), "cplaneType" : CPlaneType.LINE_ANGLE, "offset" : 25 * mm, "angle" : 0 * degree, "width" : 150 * mm, "height" : 150 * mm});
        }
    });
